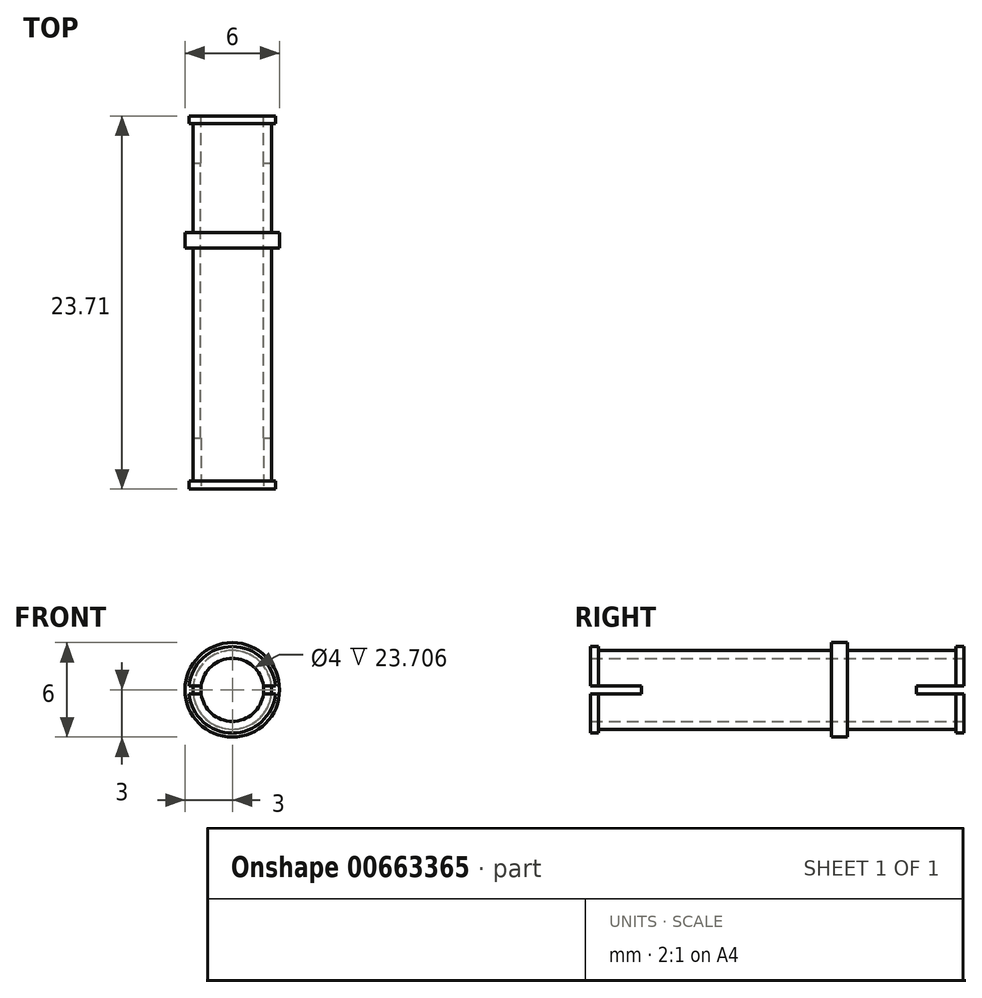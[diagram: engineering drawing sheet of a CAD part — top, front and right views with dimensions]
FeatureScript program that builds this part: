
annotation { "Feature Type Name" : "Feature", "Feature Type Description" : "" }
export const myFeature = defineFeature(function(context is Context, id is Id, definition is map)
    precondition{}
    {
        {
            var Q0;
            Q0=qCreatedBy(makeId("Front.planeOp"),FACE);
            var sketch = newSketch(context, id + "F0", { "sketchPlane" : qUnion([Q0])});
            skCircle(sketch, "E0", {"center": v(0, 0) * mm, "radius": 2.5 * mm});
            skCircle(sketch, "E1", {"center": v(0, 0) * mm, "radius": 2 * mm});
            skCircle(sketch, "E2", {"center": v(0, 0) * mm, "radius": 3 * mm});
            skSolve(sketch);
        }
        {
            var Q0;
            Q0=qSketchRegion(id+"F0",true);
            var Q1;
            Q1=makeQuery(id+"F0.imprint","IMPRINT",FACE,{"disambiguationData":[TD([[makeQuery(id+"F0.imprint","IMPRINT",EDGE,{"derivedFrom":sQuery(id+"F0.wireOp",EDGE,"E0")}),1.0]])]});
            extrude(context, id + "F1", {"entities" : qUnion([Q0, Q1]), "endBound" : BoundingType.SYMMETRIC, "depth" : 1 * mm, "offsetDistance" : 25 * mm});
        }
        {
            var Q0;
            Q0=makeQuery(id+"F1.opExtrude","CAP_FACE",FACE,{"disambiguationData":[OSD([sQuery(id+"F0.wireOp",EDGE,"E1"),sQuery(id+"F0.wireOp",EDGE,"E2")])],"isStart":false});
            var sketch = newSketch(context, id + "F2", { "sketchPlane" : qUnion([Q0])});
            skCircle(sketch, "E3", {"center": v(0, 0) * mm, "radius": 2.5 * mm});
            skSolve(sketch);
        }
        {
            var Q0;
            Q0=makeQuery(id+"F2.imprint","IMPRINT",FACE,{"disambiguationData":[TD([[makeQuery(id+"F2.imprint","IMPRINT",EDGE,{"derivedFrom":sQuery(id+"F2.wireOp",EDGE,"E3")}),1.0]])]});
            extrude(context, id + "F3", {"entities" : qUnion([Q0]), "operationType" : NewBodyOperationType.ADD, "depth" : 13.9 * mm, "offsetDistance" : 25 * mm});
        }
        {
            var Q0;
            Q0=makeQuery(id+"F1.opExtrude","CAP_FACE",FACE,{"disambiguationData":[OSD([sQuery(id+"F0.wireOp",EDGE,"E1"),sQuery(id+"F0.wireOp",EDGE,"E2")])],"isStart":true});
            var sketch = newSketch(context, id + "F4", { "sketchPlane" : qUnion([Q0])});
            skCircle(sketch, "E4", {"center": v(0, 0) * mm, "radius": 2.5 * mm});
            skSolve(sketch);
        }
        {
            var Q0;
            Q0=makeQuery(id+"F4.imprint","IMPRINT",FACE,{"disambiguationData":[TD([[makeQuery(id+"F4.imprint","IMPRINT",EDGE,{"derivedFrom":sQuery(id+"F4.wireOp",EDGE,"E4")}),1.0]])]});
            extrude(context, id + "F5", {"entities" : qUnion([Q0]), "operationType" : NewBodyOperationType.ADD, "depth" : 5.9 * mm, "offsetDistance" : 25 * mm});
        }
        {
            var Q0;
            Q0=makeQuery(id+"F5.opExtrude","CAP_FACE",FACE,{"disambiguationData":[OSD([sQuery(id+"F0.wireOp",EDGE,"E1"),sQuery(id+"F4.wireOp",EDGE,"E4")])],"isStart":false});
            var sketch = newSketch(context, id + "F6", { "sketchPlane" : qUnion([Q0])});
            skCircle(sketch, "E5", {"center": v(0, 0) * mm, "radius": 2.75 * mm});
            skSolve(sketch);
        }
        {
            var Q0;
            Q0=makeQuery(id+"F6.imprint","IMPRINT",FACE,{"disambiguationData":[TD([[makeQuery(id+"F6.imprint","IMPRINT",EDGE,{"derivedFrom":sQuery(id+"F6.wireOp",EDGE,"E5")}),1.0]])]});
            var Q1;
            Q1=makeQuery(id+"F6.imprint","IMPRINT",FACE,{"disambiguationData":[TD([[makeQuery(id+"F6.imprint","IMPRINT",EDGE,{"derivedFrom":makeQuery(id+"F5.opExtrude","CAP_EDGE",EDGE,{"disambiguationData":[OSD([sQuery(id+"F4.wireOp",EDGE,"E4")])],"isStart":false})}),1.0]])]});
            extrude(context, id + "F7", {"entities" : qUnion([Q0, Q1]), "operationType" : NewBodyOperationType.ADD, "depth" : 1 * mm, "offsetDistance" : 25 * mm});
        }
        {
            var Q0;
            Q0=makeQuery(id+"F7.opExtrude","CAP_FACE",FACE,{"disambiguationData":[OSD([sQuery(id+"F0.wireOp",EDGE,"E1"),sQuery(id+"F6.wireOp",EDGE,"E5")])],"isStart":false});
            var sketch = newSketch(context, id + "F8", { "sketchPlane" : qUnion([Q0])});
            skLineSegment(sketch, "E6.bottom", {"start": v(2.74, 0.25) * mm, "end": v(1.98, 0.25) * mm});
            skLineSegment(sketch, "E6.top", {"start": v(2.74, -0.25) * mm, "end": v(1.98, -0.25) * mm});
            skPoint(sketch, "E6.middle", {"position": v(0, 0) * mm});
            skArc(sketch, "E7.0", {"start": v(2.74, -0.25) * mm, "mid": v(2.75, 0) * mm, "end": v(2.74, 0.25) * mm});
            skArc(sketch, "E8.0", {"start": v(1.98, -0.25) * mm, "mid": v(2, 0) * mm, "end": v(1.98, 0.25) * mm});
            skLineSegment(sketch, "E9.trimOffspring", {"start": v(-1.98, 0.25) * mm, "end": v(-2.74, 0.25) * mm});
            skLineSegment(sketch, "E10.trimOffspring", {"start": v(-1.98, -0.25) * mm, "end": v(-2.74, -0.25) * mm});
            skPoint(sketch, "E11.orphan", {"position": v(-3, 0.25) * mm});
            skPoint(sketch, "E12.orphan", {"position": v(-3, -0.25) * mm});
            skPoint(sketch, "E6.left.start.orphan", {"position": v(3, 0.25) * mm});
            skArc(sketch, "E13.trimOffspring", {"start": v(-2.74, 0.25) * mm, "mid": v(-2.75, 0) * mm, "end": v(-2.74, -0.25) * mm});
            skArc(sketch, "E14.trimOffspring", {"start": v(-1.98, 0.25) * mm, "mid": v(-2, 0) * mm, "end": v(-1.98, -0.25) * mm});
            skPoint(sketch, "E15.orphan", {"position": v(3, -0.25) * mm});
            skSolve(sketch);
        }
        {
            var Q0;
            Q0=qSketchRegion(id+"F8",true);
            extrude(context, id + "F9", {"entities" : qUnion([Q0]), "operationType" : NewBodyOperationType.REMOVE, "oppositeDirection" : true, "depth" : 3 * mm, "offsetDistance" : 25 * mm});
        }
        {
            var Q0;
            Q0=makeQuery(id+"F3.opExtrude","CAP_FACE",FACE,{"disambiguationData":[OSD([sQuery(id+"F0.wireOp",EDGE,"E1"),sQuery(id+"F2.wireOp",EDGE,"E3")])],"isStart":false});
            var sketch = newSketch(context, id + "F10", { "sketchPlane" : qUnion([Q0])});
            skCircle(sketch, "E16", {"center": v(0, 0) * mm, "radius": 2.75 * mm});
            skSolve(sketch);
        }
        {
            var Q0;
            Q0=makeQuery(id+"F10.imprint","IMPRINT",FACE,{"disambiguationData":[TD([[makeQuery(id+"F10.imprint","IMPRINT",EDGE,{"derivedFrom":sQuery(id+"F10.wireOp",EDGE,"E16")}),1.0]])]});
            var Q1;
            Q1=makeQuery(id+"F10.imprint","IMPRINT",FACE,{"disambiguationData":[TD([[makeQuery(id+"F10.imprint","IMPRINT",EDGE,{"derivedFrom":makeQuery(id+"F3.opExtrude","CAP_EDGE",EDGE,{"disambiguationData":[OSD([sQuery(id+"F2.wireOp",EDGE,"E3")])],"isStart":false})}),1.0]])]});
            extrude(context, id + "F11", {"entities" : qUnion([Q0, Q1]), "operationType" : NewBodyOperationType.ADD, "depth" : 1 * mm, "offsetDistance" : 25 * mm});
        }
        {
            var Q0;
            Q0=makeQuery(id+"F11.opExtrude","CAP_FACE",FACE,{"disambiguationData":[OSD([sQuery(id+"F0.wireOp",EDGE,"E1"),sQuery(id+"F10.wireOp",EDGE,"E16")])],"isStart":false});
            var sketch = newSketch(context, id + "F12", { "sketchPlane" : qUnion([Q0])});
            skLineSegment(sketch, "E17.bottom", {"start": v(-2.74, 0.25) * mm, "end": v(-1.98, 0.25) * mm});
            skLineSegment(sketch, "E17.top", {"start": v(-2.74, -0.25) * mm, "end": v(-1.98, -0.25) * mm});
            skPoint(sketch, "E17.middle", {"position": v(0, 0) * mm});
            skArc(sketch, "E18.0", {"start": v(2.74, -0.25) * mm, "mid": v(2.75, 0) * mm, "end": v(2.74, 0.25) * mm});
            skArc(sketch, "E19.0", {"start": v(1.98, -0.25) * mm, "mid": v(2, 0) * mm, "end": v(1.98, 0.25) * mm});
            skPoint(sketch, "E20.orphan", {"position": v(-3, 0.25) * mm});
            skPoint(sketch, "E21.orphan", {"position": v(-3, -0.25) * mm});
            skLineSegment(sketch, "E22.trimOffspring", {"start": v(1.98, 0.25) * mm, "end": v(2.74, 0.25) * mm});
            skLineSegment(sketch, "E23.trimOffspring", {"start": v(1.98, -0.25) * mm, "end": v(2.74, -0.25) * mm});
            skPoint(sketch, "E24.orphan", {"position": v(3, 0.25) * mm});
            skPoint(sketch, "E25.orphan", {"position": v(3, -0.25) * mm});
            skArc(sketch, "E26.trimOffspring", {"start": v(-1.98, 0.25) * mm, "mid": v(-2, 0) * mm, "end": v(-1.98, -0.25) * mm});
            skArc(sketch, "E27.trimOffspring", {"start": v(-2.74, 0.25) * mm, "mid": v(-2.75, 0) * mm, "end": v(-2.74, -0.25) * mm});
            skSolve(sketch);
        }
        {
            var Q0;
            Q0=qSketchRegion(id+"F12",true);
            extrude(context, id + "F13", {"entities" : qUnion([Q0]), "operationType" : NewBodyOperationType.REMOVE, "oppositeDirection" : true, "depth" : 3 * mm, "offsetDistance" : 25 * mm});
        }
        {
            var Q0;
            {var subQ0=sQuery(id+"F0.wireOp",EDGE,"E1");var subQ1=sQuery(id+"F10.wireOp",EDGE,"E16");Q0=makeQuery(id+"F13.boolean.opBoolean","SPLIT",FACE,{"disambiguationData":[TD([makeQuery(id+"F13.opExtrude","SWEPT_FACE",FACE,{"disambiguationData":[OSD([sQuery(id+"F12.wireOp",EDGE,"E17.bottom")])]})])],"derivedFrom":makeQuery(id+"F11.opExtrude","CAP_FACE",FACE,{"disambiguationData":[OSD([subQ0,subQ1])],"isStart":false})});}
            var Q1;
            {var subQ0=sQuery(id+"F0.wireOp",EDGE,"E1");var subQ1=sQuery(id+"F10.wireOp",EDGE,"E16");Q1=makeQuery(id+"F13.boolean.opBoolean","SPLIT",FACE,{"disambiguationData":[TD([makeQuery(id+"F13.opExtrude","SWEPT_FACE",FACE,{"disambiguationData":[OSD([sQuery(id+"F12.wireOp",EDGE,"E17.top")])]})])],"derivedFrom":makeQuery(id+"F11.opExtrude","CAP_FACE",FACE,{"disambiguationData":[OSD([subQ0,subQ1])],"isStart":false})});}
            var Q2;
            Q2=makeQuery(id+"F13.boolean.opBoolean","COPY",FACE,{"derivedFrom":makeQuery(id+"F13.opExtrude","CAP_FACE",FACE,{"disambiguationData":[OSD([sQuery(id+"F12.wireOp",EDGE,"E17.bottom"),sQuery(id+"F12.wireOp",EDGE,"E17.top"),sQuery(id+"F12.wireOp",EDGE,"E26.trimOffspring"),sQuery(id+"F12.wireOp",EDGE,"E27.trimOffspring")])],"isStart":false})});
            var Q3;
            Q3=makeQuery(id+"F13.boolean.opBoolean","COPY",FACE,{"derivedFrom":makeQuery(id+"F13.opExtrude","CAP_FACE",FACE,{"disambiguationData":[OSD([sQuery(id+"F12.wireOp",EDGE,"E18.0"),sQuery(id+"F12.wireOp",EDGE,"E19.0"),sQuery(id+"F12.wireOp",EDGE,"E22.trimOffspring"),sQuery(id+"F12.wireOp",EDGE,"E23.trimOffspring")])],"isStart":false})});
            extrude(context, id + "F14", {"entities" : qUnion([Q0, Q1, Q2, Q3]), "operationType" : NewBodyOperationType.ADD, "depth" : 0.16 * mm, "offsetDistance" : 25 * mm});
        }
        {
            var Q0;
            {var subQ0=sQuery(id+"F6.wireOp",EDGE,"E5");var subQ1=sQuery(id+"F0.wireOp",EDGE,"E1");Q0=makeQuery(id+"F9.boolean.opBoolean","SPLIT",FACE,{"disambiguationData":[TD([makeQuery(id+"F9.opExtrude","SWEPT_FACE",FACE,{"disambiguationData":[OSD([sQuery(id+"F8.wireOp",EDGE,"E6.bottom")])]})])],"derivedFrom":makeQuery(id+"F7.opExtrude","CAP_FACE",FACE,{"disambiguationData":[OSD([subQ1,subQ0])],"isStart":false})});}
            var Q1;
            {var subQ0=sQuery(id+"F6.wireOp",EDGE,"E5");var subQ1=sQuery(id+"F0.wireOp",EDGE,"E1");Q1=makeQuery(id+"F9.boolean.opBoolean","SPLIT",FACE,{"disambiguationData":[TD([makeQuery(id+"F9.opExtrude","SWEPT_FACE",FACE,{"disambiguationData":[OSD([sQuery(id+"F8.wireOp",EDGE,"E6.top")])]})])],"derivedFrom":makeQuery(id+"F7.opExtrude","CAP_FACE",FACE,{"disambiguationData":[OSD([subQ1,subQ0])],"isStart":false})});}
            var Q2;
            Q2=makeQuery(id+"F9.boolean.opBoolean","COPY",FACE,{"derivedFrom":makeQuery(id+"F9.opExtrude","CAP_FACE",FACE,{"disambiguationData":[OSD([sQuery(id+"F8.wireOp",EDGE,"E6.bottom"),sQuery(id+"F8.wireOp",EDGE,"E6.top"),sQuery(id+"F8.wireOp",EDGE,"E7.0"),sQuery(id+"F8.wireOp",EDGE,"E8.0")])],"isStart":false})});
            var Q3;
            Q3=makeQuery(id+"F9.boolean.opBoolean","COPY",FACE,{"derivedFrom":makeQuery(id+"F9.opExtrude","CAP_FACE",FACE,{"disambiguationData":[OSD([sQuery(id+"F8.wireOp",EDGE,"E9.trimOffspring"),sQuery(id+"F8.wireOp",EDGE,"E10.trimOffspring"),sQuery(id+"F8.wireOp",EDGE,"E13.trimOffspring"),sQuery(id+"F8.wireOp",EDGE,"E14.trimOffspring")])],"isStart":false})});
            extrude(context, id + "F15", {"entities" : qUnion([Q0, Q1, Q2, Q3]), "operationType" : NewBodyOperationType.ADD, "depth" : 0 * mm, "offsetDistance" : 25 * mm});
        }
        {
            var Q0;
            {var subQ0=sQuery(id+"F10.wireOp",EDGE,"E16");Q0=makeQuery(id+"F13.boolean.opBoolean","SPLIT",FACE,{"disambiguationData":[TD([makeQuery(id+"F13.opExtrude","SWEPT_FACE",FACE,{"disambiguationData":[OSD([sQuery(id+"F12.wireOp",EDGE,"E17.top")])]})])],"derivedFrom":makeQuery(id+"F11.opExtrude","CAP_FACE",FACE,{"disambiguationData":[OSD([sQuery(id+"F0.wireOp",EDGE,"E1"),subQ0])],"isStart":true})});}
            var Q1;
            {var subQ0=sQuery(id+"F10.wireOp",EDGE,"E16");Q1=makeQuery(id+"F13.boolean.opBoolean","SPLIT",FACE,{"disambiguationData":[TD([makeQuery(id+"F13.opExtrude","SWEPT_FACE",FACE,{"disambiguationData":[OSD([sQuery(id+"F12.wireOp",EDGE,"E17.bottom")])]})])],"derivedFrom":makeQuery(id+"F11.opExtrude","CAP_FACE",FACE,{"disambiguationData":[OSD([sQuery(id+"F0.wireOp",EDGE,"E1"),subQ0])],"isStart":true})});}
            extrude(context, id + "F16", {"entities" : qUnion([Q0, Q1]), "operationType" : NewBodyOperationType.REMOVE, "oppositeDirection" : true, "depth" : 0.66 * mm, "offsetDistance" : 25 * mm});
        }
        {
            var Q0;
            {var subQ0=sQuery(id+"F6.wireOp",EDGE,"E5");Q0=makeQuery(id+"F9.boolean.opBoolean","SPLIT",FACE,{"disambiguationData":[TD([makeQuery(id+"F9.opExtrude","SWEPT_FACE",FACE,{"disambiguationData":[OSD([sQuery(id+"F8.wireOp",EDGE,"E6.bottom")])]})])],"derivedFrom":makeQuery(id+"F7.opExtrude","CAP_FACE",FACE,{"disambiguationData":[OSD([sQuery(id+"F0.wireOp",EDGE,"E1"),subQ0])],"isStart":true})});}
            var Q1;
            {var subQ0=sQuery(id+"F6.wireOp",EDGE,"E5");Q1=makeQuery(id+"F9.boolean.opBoolean","SPLIT",FACE,{"disambiguationData":[TD([makeQuery(id+"F9.opExtrude","SWEPT_FACE",FACE,{"disambiguationData":[OSD([sQuery(id+"F8.wireOp",EDGE,"E6.top")])]})])],"derivedFrom":makeQuery(id+"F7.opExtrude","CAP_FACE",FACE,{"disambiguationData":[OSD([sQuery(id+"F0.wireOp",EDGE,"E1"),subQ0])],"isStart":true})});}
            extrude(context, id + "F17", {"entities" : qUnion([Q0, Q1]), "operationType" : NewBodyOperationType.REMOVE, "oppositeDirection" : true, "depth" : 0.66 * mm, "offsetDistance" : 25 * mm});
        }
        {
            var Q0;
            {var subQ0=sQuery(id+"F0.wireOp",EDGE,"E1");var subQ1=sQuery(id+"F10.wireOp",EDGE,"E16");Q0=makeQuery(id+"F14.opExtrude","CAP_FACE",FACE,{"disambiguationData":[OSD([subQ0,subQ1]),TDD([makeQuery(id+"F13.boolean.opBoolean","SPLIT",FACE,{"disambiguationData":[TD([makeQuery(id+"F13.opExtrude","SWEPT_FACE",FACE,{"disambiguationData":[OSD([sQuery(id+"F12.wireOp",EDGE,"E17.bottom")])]})])],"derivedFrom":makeQuery(id+"F11.opExtrude","CAP_FACE",FACE,{"disambiguationData":[OSD([subQ0,subQ1])],"isStart":false})})])],"isStart":false});}
            var Q1;
            {var subQ0=sQuery(id+"F0.wireOp",EDGE,"E1");var subQ1=sQuery(id+"F10.wireOp",EDGE,"E16");Q1=makeQuery(id+"F14.opExtrude","CAP_FACE",FACE,{"disambiguationData":[OSD([subQ0,subQ1]),TDD([makeQuery(id+"F13.boolean.opBoolean","SPLIT",FACE,{"disambiguationData":[TD([makeQuery(id+"F13.opExtrude","SWEPT_FACE",FACE,{"disambiguationData":[OSD([sQuery(id+"F12.wireOp",EDGE,"E17.top")])]})])],"derivedFrom":makeQuery(id+"F11.opExtrude","CAP_FACE",FACE,{"disambiguationData":[OSD([subQ0,subQ1])],"isStart":false})})])],"isStart":false});}
            var Q2;
            Q2=makeQuery(id+"F14.opExtrude","CAP_FACE",FACE,{"disambiguationData":[OSD([sQuery(id+"F12.wireOp",EDGE,"E17.bottom"),sQuery(id+"F12.wireOp",EDGE,"E17.top"),sQuery(id+"F12.wireOp",EDGE,"E26.trimOffspring"),sQuery(id+"F12.wireOp",EDGE,"E27.trimOffspring")])],"isStart":false});
            var Q3;
            Q3=makeQuery(id+"F14.opExtrude","CAP_FACE",FACE,{"disambiguationData":[OSD([sQuery(id+"F12.wireOp",EDGE,"E18.0"),sQuery(id+"F12.wireOp",EDGE,"E19.0"),sQuery(id+"F12.wireOp",EDGE,"E22.trimOffspring"),sQuery(id+"F12.wireOp",EDGE,"E23.trimOffspring")])],"isStart":false});
            extrude(context, id + "F18", {"entities" : qUnion([Q0, Q1, Q2, Q3]), "operationType" : NewBodyOperationType.ADD, "depth" : 0 * mm, "offsetDistance" : 25 * mm});
        }
        {
            var Q0;
            {var subQ0=sQuery(id+"F0.wireOp",EDGE,"E1");var subQ1=sQuery(id+"F10.wireOp",EDGE,"E16");Q0=makeQuery(id+"F18.opExtrude","CAP_FACE",FACE,{"disambiguationData":[OSD([subQ0,subQ1]),TDD([makeQuery(id+"F14.opExtrude","CAP_FACE",FACE,{"disambiguationData":[OSD([subQ0,subQ1]),TDD([makeQuery(id+"F13.boolean.opBoolean","SPLIT",FACE,{"disambiguationData":[TD([makeQuery(id+"F13.opExtrude","SWEPT_FACE",FACE,{"disambiguationData":[OSD([sQuery(id+"F12.wireOp",EDGE,"E17.bottom")])]})])],"derivedFrom":makeQuery(id+"F11.opExtrude","CAP_FACE",FACE,{"disambiguationData":[OSD([subQ0,subQ1])],"isStart":false})})])],"isStart":false})])],"isStart":false});}
            var Q1;
            {var subQ0=sQuery(id+"F0.wireOp",EDGE,"E1");var subQ1=sQuery(id+"F10.wireOp",EDGE,"E16");Q1=makeQuery(id+"F18.opExtrude","CAP_FACE",FACE,{"disambiguationData":[OSD([subQ0,subQ1]),TDD([makeQuery(id+"F14.opExtrude","CAP_FACE",FACE,{"disambiguationData":[OSD([subQ0,subQ1]),TDD([makeQuery(id+"F13.boolean.opBoolean","SPLIT",FACE,{"disambiguationData":[TD([makeQuery(id+"F13.opExtrude","SWEPT_FACE",FACE,{"disambiguationData":[OSD([sQuery(id+"F12.wireOp",EDGE,"E17.top")])]})])],"derivedFrom":makeQuery(id+"F11.opExtrude","CAP_FACE",FACE,{"disambiguationData":[OSD([subQ0,subQ1])],"isStart":false})})])],"isStart":false})])],"isStart":false});}
            extrude(context, id + "F19", {"entities" : qUnion([Q0, Q1]), "operationType" : NewBodyOperationType.ADD, "depth" : 0.24 * mm, "offsetDistance" : 25 * mm});
        }
        {
            var Q0;
            {var subQ0=sQuery(id+"F10.wireOp",EDGE,"E16");var subQ1=sQuery(id+"F0.wireOp",EDGE,"E1");Q0=makeQuery(id+"F16.boolean.opBoolean","COPY",FACE,{"derivedFrom":makeQuery(id+"F16.opExtrude","CAP_FACE",FACE,{"disambiguationData":[OSD([subQ1,subQ0]),TDD([makeQuery(id+"F13.boolean.opBoolean","SPLIT",FACE,{"disambiguationData":[TD([makeQuery(id+"F13.opExtrude","SWEPT_FACE",FACE,{"disambiguationData":[OSD([sQuery(id+"F12.wireOp",EDGE,"E17.bottom")])]})])],"derivedFrom":makeQuery(id+"F11.opExtrude","CAP_FACE",FACE,{"disambiguationData":[OSD([subQ1,subQ0])],"isStart":true})})])],"isStart":false})});}
            var Q1;
            {var subQ0=sQuery(id+"F10.wireOp",EDGE,"E16");var subQ1=sQuery(id+"F0.wireOp",EDGE,"E1");Q1=makeQuery(id+"F16.boolean.opBoolean","COPY",FACE,{"derivedFrom":makeQuery(id+"F16.opExtrude","CAP_FACE",FACE,{"disambiguationData":[OSD([subQ1,subQ0]),TDD([makeQuery(id+"F13.boolean.opBoolean","SPLIT",FACE,{"disambiguationData":[TD([makeQuery(id+"F13.opExtrude","SWEPT_FACE",FACE,{"disambiguationData":[OSD([sQuery(id+"F12.wireOp",EDGE,"E17.top")])]})])],"derivedFrom":makeQuery(id+"F11.opExtrude","CAP_FACE",FACE,{"disambiguationData":[OSD([subQ1,subQ0])],"isStart":true})})])],"isStart":false})});}
            extrude(context, id + "F20", {"entities" : qUnion([Q0, Q1]), "operationType" : NewBodyOperationType.REMOVE, "oppositeDirection" : true, "depth" : 0.24 * mm, "offsetDistance" : 25 * mm});
        }
        {
            var Q0;
            {var subQ0=sQuery(id+"F6.wireOp",EDGE,"E5");var subQ1=sQuery(id+"F0.wireOp",EDGE,"E1");Q0=makeQuery(id+"F15.opExtrude","CAP_FACE",FACE,{"disambiguationData":[OSD([subQ1,subQ0]),TDD([makeQuery(id+"F9.boolean.opBoolean","SPLIT",FACE,{"disambiguationData":[TD([makeQuery(id+"F9.opExtrude","SWEPT_FACE",FACE,{"disambiguationData":[OSD([sQuery(id+"F8.wireOp",EDGE,"E6.top")])]})])],"derivedFrom":makeQuery(id+"F7.opExtrude","CAP_FACE",FACE,{"disambiguationData":[OSD([subQ1,subQ0])],"isStart":false})})])],"isStart":false});}
            var Q1;
            {var subQ0=sQuery(id+"F6.wireOp",EDGE,"E5");var subQ1=sQuery(id+"F0.wireOp",EDGE,"E1");Q1=makeQuery(id+"F15.opExtrude","CAP_FACE",FACE,{"disambiguationData":[OSD([subQ1,subQ0]),TDD([makeQuery(id+"F9.boolean.opBoolean","SPLIT",FACE,{"disambiguationData":[TD([makeQuery(id+"F9.opExtrude","SWEPT_FACE",FACE,{"disambiguationData":[OSD([sQuery(id+"F8.wireOp",EDGE,"E6.bottom")])]})])],"derivedFrom":makeQuery(id+"F7.opExtrude","CAP_FACE",FACE,{"disambiguationData":[OSD([subQ1,subQ0])],"isStart":false})})])],"isStart":false});}
            var Q2;
            Q2=makeQuery(id+"F15.opExtrude","CAP_FACE",FACE,{"disambiguationData":[OSD([sQuery(id+"F8.wireOp",EDGE,"E6.bottom"),sQuery(id+"F8.wireOp",EDGE,"E6.top"),sQuery(id+"F8.wireOp",EDGE,"E7.0"),sQuery(id+"F8.wireOp",EDGE,"E8.0")])],"isStart":false});
            var Q3;
            Q3=makeQuery(id+"F15.opExtrude","CAP_FACE",FACE,{"disambiguationData":[OSD([sQuery(id+"F8.wireOp",EDGE,"E9.trimOffspring"),sQuery(id+"F8.wireOp",EDGE,"E10.trimOffspring"),sQuery(id+"F8.wireOp",EDGE,"E13.trimOffspring"),sQuery(id+"F8.wireOp",EDGE,"E14.trimOffspring")])],"isStart":false});
            extrude(context, id + "F21", {"entities" : qUnion([Q0, Q1, Q2, Q3]), "operationType" : NewBodyOperationType.ADD, "depth" : .5 * mm, "offsetDistance" : 25 * mm});
        }
        {
            var Q0;
            {var subQ0=sQuery(id+"F6.wireOp",EDGE,"E5");var subQ1=sQuery(id+"F0.wireOp",EDGE,"E1");Q0=makeQuery(id+"F17.boolean.opBoolean","COPY",FACE,{"derivedFrom":makeQuery(id+"F17.opExtrude","CAP_FACE",FACE,{"disambiguationData":[OSD([subQ1,subQ0]),TDD([makeQuery(id+"F9.boolean.opBoolean","SPLIT",FACE,{"disambiguationData":[TD([makeQuery(id+"F9.opExtrude","SWEPT_FACE",FACE,{"disambiguationData":[OSD([sQuery(id+"F8.wireOp",EDGE,"E6.top")])]})])],"derivedFrom":makeQuery(id+"F7.opExtrude","CAP_FACE",FACE,{"disambiguationData":[OSD([subQ1,subQ0])],"isStart":true})})])],"isStart":false})});}
            var Q1;
            {var subQ0=sQuery(id+"F6.wireOp",EDGE,"E5");var subQ1=sQuery(id+"F0.wireOp",EDGE,"E1");Q1=makeQuery(id+"F17.boolean.opBoolean","COPY",FACE,{"derivedFrom":makeQuery(id+"F17.opExtrude","CAP_FACE",FACE,{"disambiguationData":[OSD([subQ1,subQ0]),TDD([makeQuery(id+"F9.boolean.opBoolean","SPLIT",FACE,{"disambiguationData":[TD([makeQuery(id+"F9.opExtrude","SWEPT_FACE",FACE,{"disambiguationData":[OSD([sQuery(id+"F8.wireOp",EDGE,"E6.bottom")])]})])],"derivedFrom":makeQuery(id+"F7.opExtrude","CAP_FACE",FACE,{"disambiguationData":[OSD([subQ1,subQ0])],"isStart":true})})])],"isStart":false})});}
            extrude(context, id + "F22", {"entities" : qUnion([Q0, Q1]), "operationType" : NewBodyOperationType.REMOVE, "oppositeDirection" : true, "depth" : .35 * mm, "offsetDistance" : 25 * mm});
        }
    });
